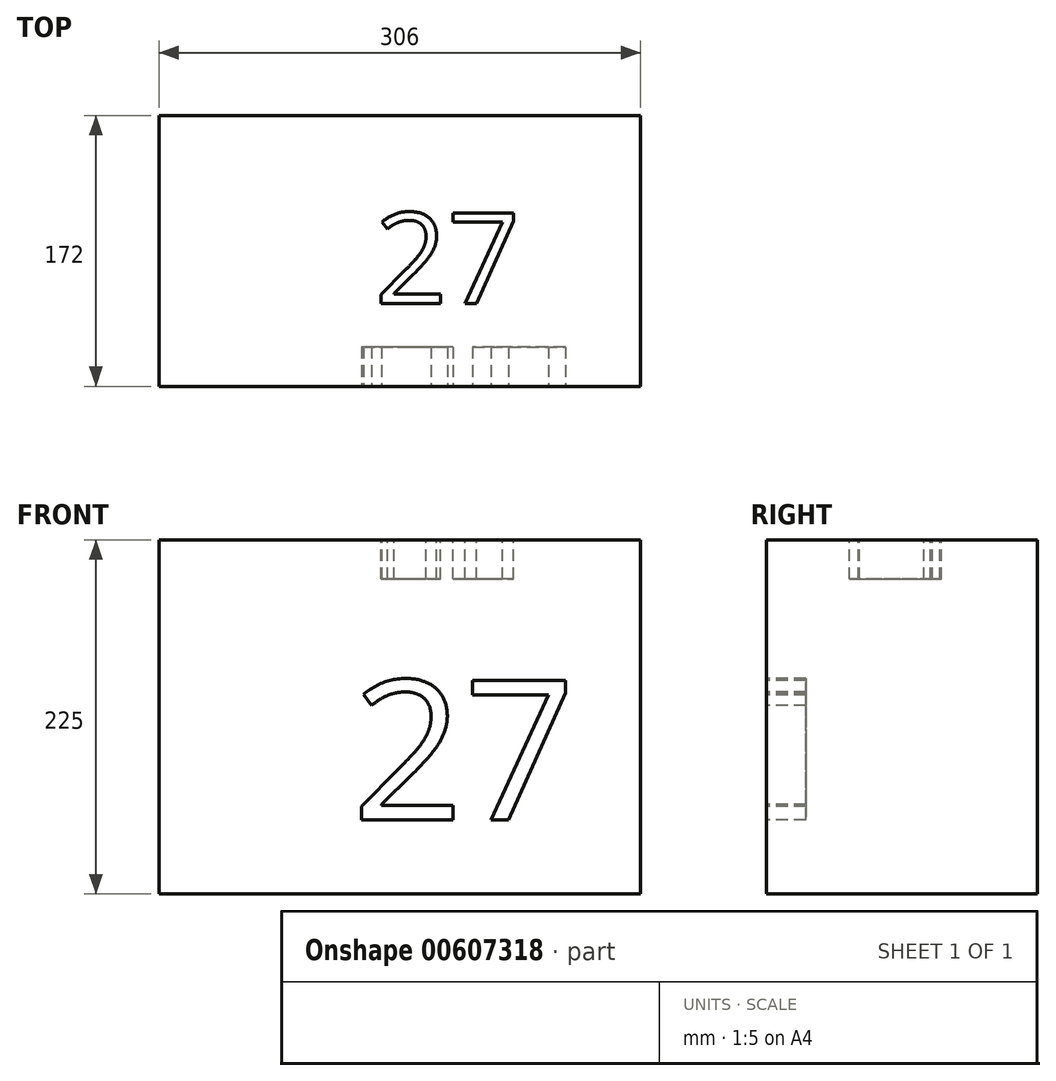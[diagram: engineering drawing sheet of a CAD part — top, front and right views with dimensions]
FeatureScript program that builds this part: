
annotation { "Feature Type Name" : "Feature", "Feature Type Description" : "" }
export const myFeature = defineFeature(function(context is Context, id is Id, definition is map)
    precondition{}
    {
        {
            var Q0;
            Q0=qCreatedBy(makeId("Top.planeOp"),FACE);
            var sketch = newSketch(context, id + "F0", { "sketchPlane" : qUnion([Q0])});
            skLineSegment(sketch, "E0.bottom", {"start": v(0, 0) * mm, "end": v(306, 0) * mm});
            skLineSegment(sketch, "E0.top", {"start": v(0, 172) * mm, "end": v(306, 172) * mm});
            skLineSegment(sketch, "E0.left", {"start": v(0, 0) * mm, "end": v(0, 172) * mm});
            skLineSegment(sketch, "E0.right", {"start": v(306, 0) * mm, "end": v(306, 172) * mm});
            skSolve(sketch);
        }
        {
            var Q0;
            Q0 = qSketchRegion(id + "F0", true);
            extrude(context, id + "F1", {"entities" : qUnion([Q0]), "depth" : 225 * mm, "offsetDistance" : 25.4 * mm});
        }
        {
            var Q0;
            Q0=makeQuery(id+"F1.opExtrude","SWEPT_FACE",FACE,{"disambiguationData":[OSD([sQuery(id+"F0.wireOp",EDGE,"E0.bottom")])]});
            var sketch = newSketch(context, id + "F2", { "sketchPlane" : qUnion([Q0])});
            skText(sketch, "E1", { "text": "27", "fontName": "OpenSans-Regular.ttf"});
            const initialGuessF2  = {"E1": [0.12263, 0.04708, 1, 0, 0.08933]};
            skSetInitialGuess(sketch, initialGuessF2);
            skSolve(sketch);
        }
        {
            var Q0;
            Q0 = qSketchRegion(id + "F2", true);
            extrude(context, id + "F3", {"entities" : qUnion([Q0]), "operationType" : NewBodyOperationType.REMOVE, "oppositeDirection" : true, "depth" : 25 * mm, "offsetDistance" : 25 * mm});
        }
        {
            var Q0;
            Q0=makeQuery(id+"F1.opExtrude","CAP_FACE",FACE,{"disambiguationData":[OSD([sQuery(id+"F0.wireOp",EDGE,"E0.bottom"),sQuery(id+"F0.wireOp",EDGE,"E0.top"),sQuery(id+"F0.wireOp",EDGE,"E0.left"),sQuery(id+"F0.wireOp",EDGE,"E0.right")])],"isStart":false});
            var sketch = newSketch(context, id + "F4", { "sketchPlane" : qUnion([Q0])});
            skText(sketch, "E2", { "text": "27\n", "fontName": "OpenSans-Regular.ttf"});
            const initialGuessF4  = {"E2": [0.13701, 0.05257, 1, 0, 0.0581]};
            skSetInitialGuess(sketch, initialGuessF4);
            skSolve(sketch);
        }
        {
            var Q0;
            Q0 = qSketchRegion(id + "F4", true);
            extrude(context, id + "F5", {"entities" : qUnion([Q0]), "operationType" : NewBodyOperationType.REMOVE, "oppositeDirection" : true, "depth" : 25 * mm, "offsetDistance" : 25 * mm});
        }
    });
